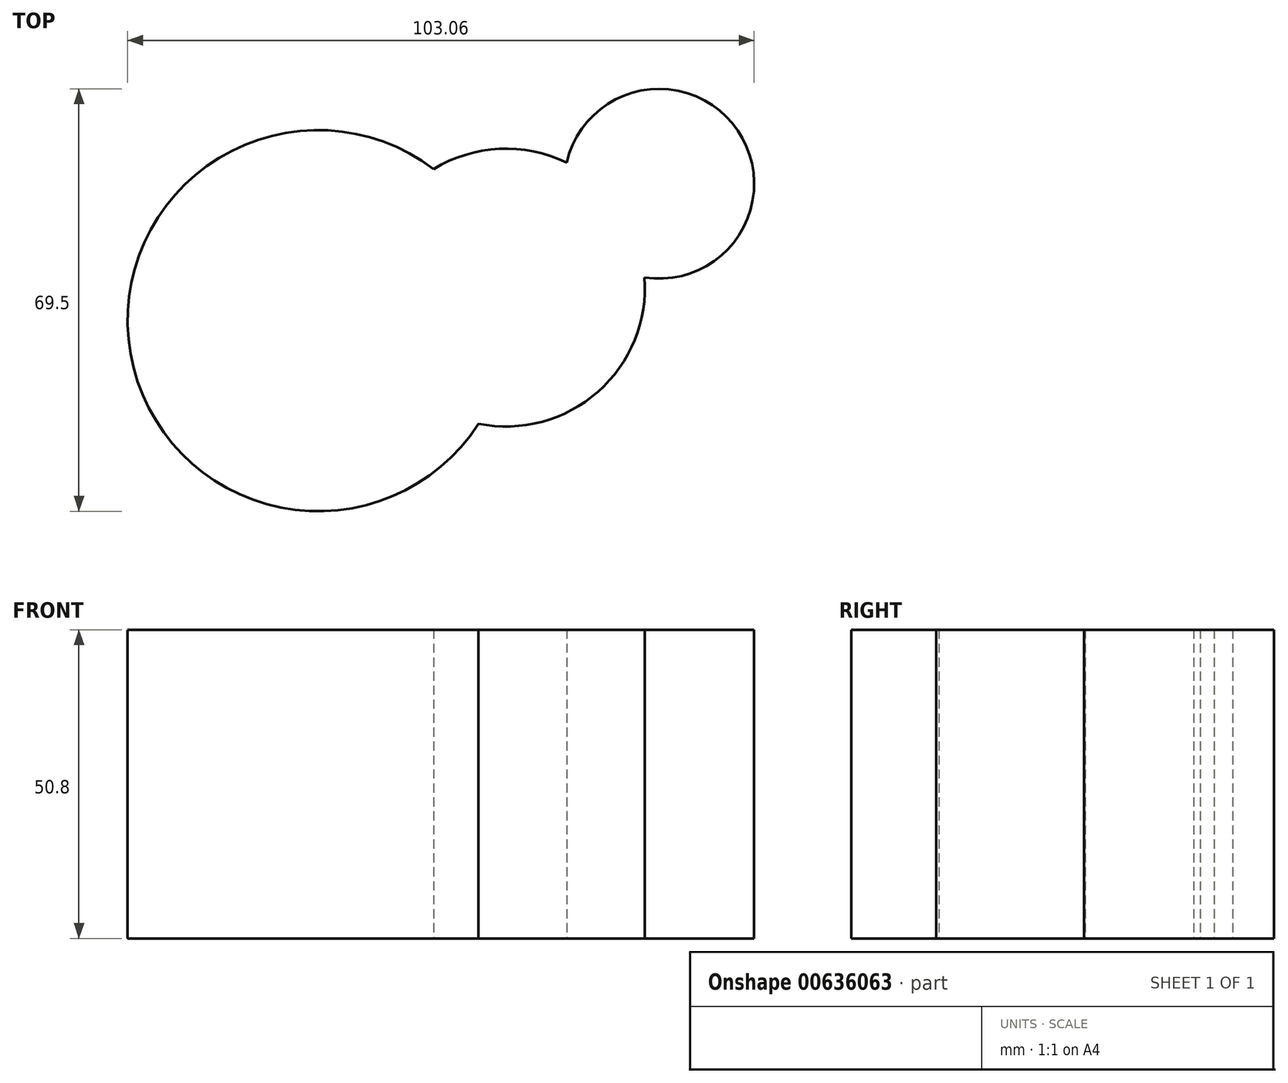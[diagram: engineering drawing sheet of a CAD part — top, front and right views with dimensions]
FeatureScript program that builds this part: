
annotation { "Feature Type Name" : "Feature", "Feature Type Description" : "" }
export const myFeature = defineFeature(function(context is Context, id is Id, definition is map)
    precondition{}
    {
        {
            var Q0;
            Q0=qCreatedBy(makeId("Top.planeOp"),FACE);
            var sketch = newSketch(context, id + "F0", { "sketchPlane" : qUnion([Q0])});
            skCircle(sketch, "E0", {"center": v(0, 0) * mm, "radius": 30.25 * mm});
            skCircle(sketch, "E1", {"center": v(0, 0) * mm, "radius": 31.36 * mm});
            skCircle(sketch, "E2", {"center": v(30.88, 5.45) * mm, "radius": 22.86 * mm});
            skCircle(sketch, "E3", {"center": v(56.09, 22.53) * mm, "radius": 15.61 * mm});
            skSolve(sketch);
        }
        {
            var Q0;
            {var subQ0=sQuery(id+"F0.wireOp",EDGE,"E3");var subQ1=sQuery(id+"F0.wireOp",EDGE,"E2");var subQ2=makeQuery(id+"F0.imprint","INTERSECT",VERTEX,{"disambiguationData":[OD(0.0)],"derivedFrom":[subQ1,subQ0]});Q0=makeQuery(id+"F0.imprint","IMPRINT",FACE,{"disambiguationData":[TD([[makeQuery(id+"F0.imprint","IMPRINT",EDGE,{"disambiguationData":[TD([[subQ2,1.0]])],"derivedFrom":subQ1}),-1.0]])]});}
            var Q1;
            {var subQ0=sQuery(id+"F0.wireOp",EDGE,"E2");var subQ1=sQuery(id+"F0.wireOp",EDGE,"E1");var subQ2=makeQuery(id+"F0.imprint","INTERSECT",VERTEX,{"disambiguationData":[OD(0.0)],"derivedFrom":[subQ1,subQ0]});Q1=makeQuery(id+"F0.imprint","IMPRINT",FACE,{"disambiguationData":[TD([[makeQuery(id+"F0.imprint","IMPRINT",EDGE,{"disambiguationData":[TD([[subQ2,1.0]])],"derivedFrom":subQ1}),-1.0]])]});}
            var Q2;
            {var subQ0=sQuery(id+"F0.wireOp",EDGE,"E3");var subQ1=sQuery(id+"F0.wireOp",EDGE,"E2");var subQ2=makeQuery(id+"F0.imprint","INTERSECT",VERTEX,{"disambiguationData":[OD(0.0)],"derivedFrom":[subQ1,subQ0]});Q2=makeQuery(id+"F0.imprint","IMPRINT",FACE,{"disambiguationData":[TD([[makeQuery(id+"F0.imprint","IMPRINT",EDGE,{"disambiguationData":[TD([[subQ2,1.0]])],"derivedFrom":subQ1}),1.0]])]});}
            var Q3;
            {var subQ0=sQuery(id+"F0.wireOp",EDGE,"E2");var subQ1=sQuery(id+"F0.wireOp",EDGE,"E0");var subQ2=makeQuery(id+"F0.imprint","INTERSECT",VERTEX,{"disambiguationData":[OD(0.0)],"derivedFrom":[subQ1,subQ0]});Q3=makeQuery(id+"F0.imprint","IMPRINT",FACE,{"disambiguationData":[TD([[makeQuery(id+"F0.imprint","IMPRINT",EDGE,{"disambiguationData":[TD([[subQ2,1.0]])],"derivedFrom":subQ1}),1.0]])]});}
            var Q4;
            Q4 = qSketchRegion(id + "F0", true);
            var Q5;
            {var subQ0=sQuery(id+"F0.wireOp",EDGE,"E2");var subQ1=sQuery(id+"F0.wireOp",EDGE,"E0");var subQ2=makeQuery(id+"F0.imprint","INTERSECT",VERTEX,{"disambiguationData":[OD(0.0)],"derivedFrom":[subQ1,subQ0]});Q5=makeQuery(id+"F0.imprint","IMPRINT",FACE,{"disambiguationData":[TD([[makeQuery(id+"F0.imprint","IMPRINT",EDGE,{"disambiguationData":[TD([[subQ2,-1.0]])],"derivedFrom":subQ1}),1.0]])]});}
            extrude(context, id + "F1", {"entities" : qUnion([Q0, Q1, Q2, Q3, Q4, Q5]), "depth" : 50.8 * mm, "offsetDistance" : 25.4 * mm});
        }
        {
            var Q0;
            Q0=qCreatedBy(makeId("Top.planeOp"),FACE);
            var sketch = newSketch(context, id + "F2", { "sketchPlane" : qUnion([Q0])});
            skCircle(sketch, "E4", {"center": v(38.62, 0) * mm, "radius": 10.1 * mm});
            skSolve(sketch);
        }
        {
            var Q0;
            Q0=sQuery(id+"F2.wireOp",EDGE,"E4");
            extrude(context, id + "F3", {"bodyType" : ToolBodyType.SURFACE, "surfaceEntities" : qUnion([Q0]), "depth" : 50.8 * mm, "offsetDistance" : 25.4 * mm});
        }
    });
